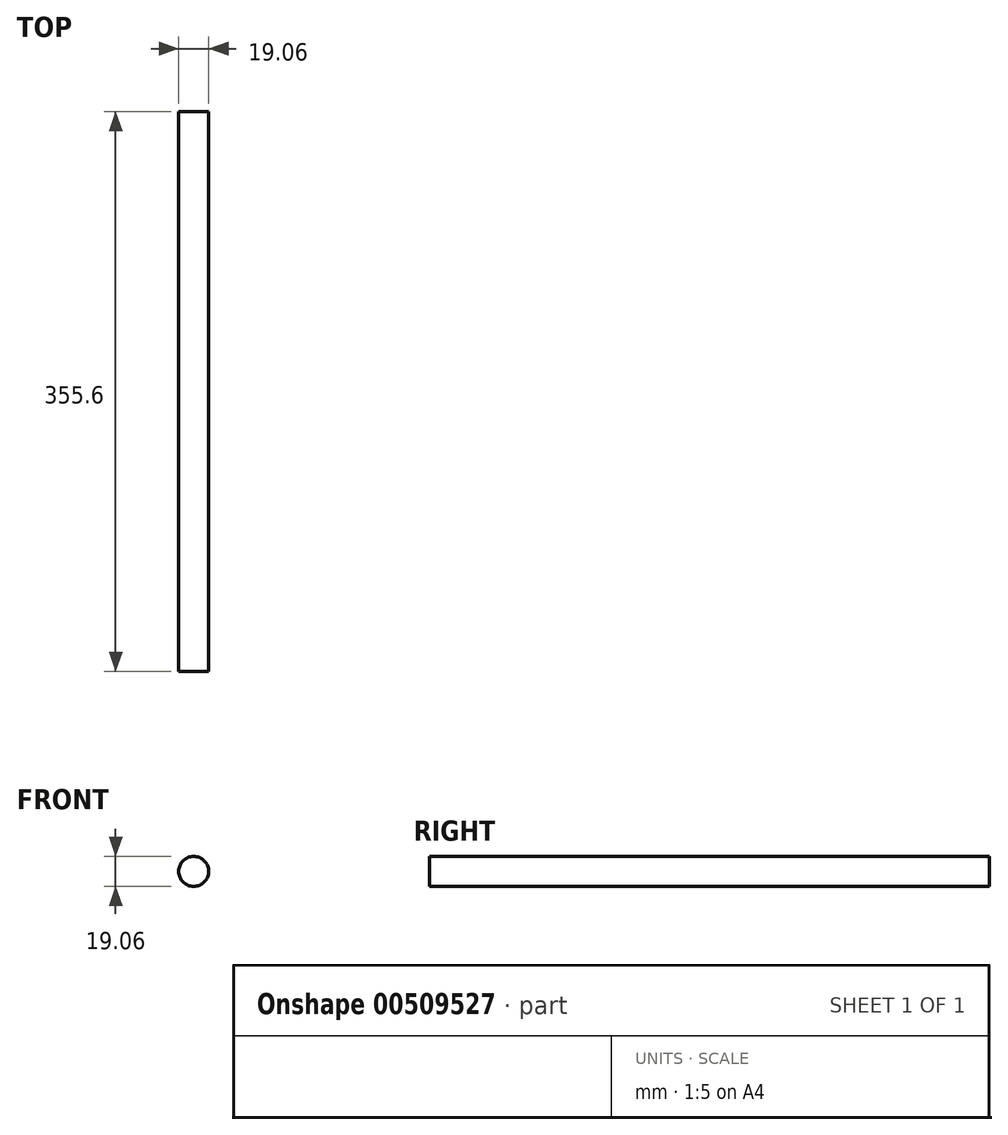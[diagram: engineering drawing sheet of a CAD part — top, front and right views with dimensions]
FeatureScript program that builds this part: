
annotation { "Feature Type Name" : "Feature", "Feature Type Description" : "" }
export const myFeature = defineFeature(function(context is Context, id is Id, definition is map)
    precondition{}
    {
        {
            var Q0;
            Q0=qCreatedBy(makeId("Top.planeOp"),FACE);
            var sketch = newSketch(context, id + "F0", { "sketchPlane" : qUnion([Q0])});
            skLineSegment(sketch, "E0.bottom", {"start": v(9.52, 177.8) * mm, "end": v(-9.52, 177.8) * mm});
            skLineSegment(sketch, "E0.top", {"start": v(9.53, -177.8) * mm, "end": v(-9.53, -177.8) * mm});
            skLineSegment(sketch, "E0.left", {"start": v(9.53, 177.8) * mm, "end": v(9.53, -177.8) * mm});
            skLineSegment(sketch, "E0.right", {"start": v(-9.52, 177.8) * mm, "end": v(-9.53, -177.8) * mm});
            skPoint(sketch, "E0.middle", {"position": v(0, 0) * mm});
            skLineSegment(sketch, "E1", {"start": v(0, -177.8) * mm, "end": v(0, 177.8) * mm});
            skSolve(sketch);
        }
        {
            var Q0;
            {var subQ0=sQuery(id+"F0.wireOp",EDGE,"E0.right");Q0=makeQuery(id+"F0.imprint","IMPRINT",FACE,{"disambiguationData":[TD([[makeQuery(id+"F0.imprint","IMPRINT",EDGE,{"derivedFrom":subQ0}),1.0]])]});}
            var Q1;
            Q1=sQuery(id+"F0.wireOp",EDGE,"E1");
            revolve(context, id + "F1", {"entities" : qUnion([Q0]), "axis" : qUnion([Q1]), "revolveType" : RevolveType.FULL});
        }
    });
